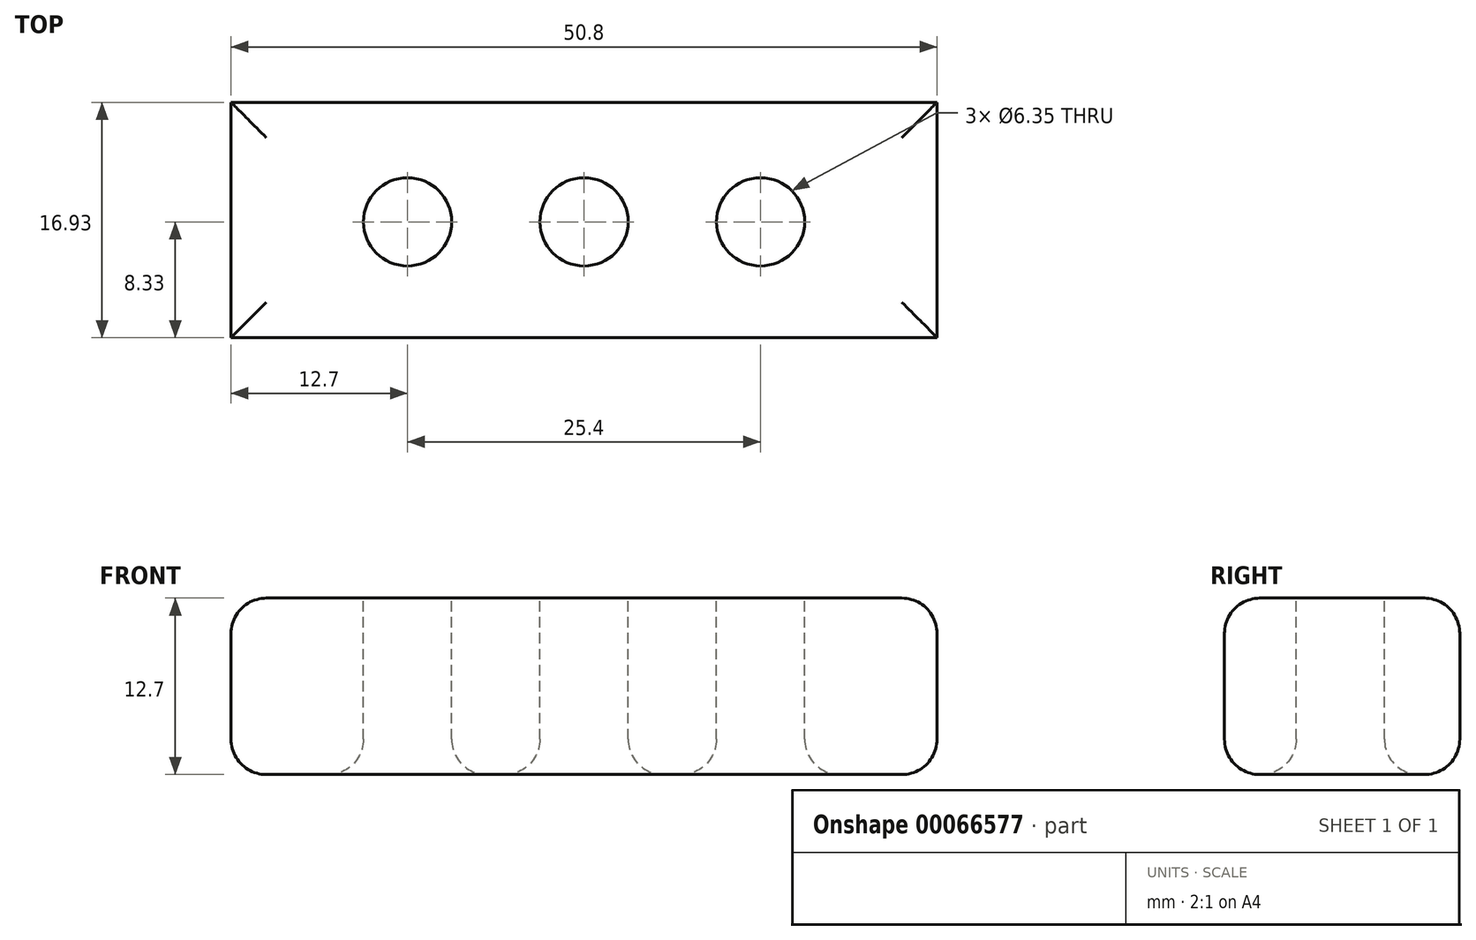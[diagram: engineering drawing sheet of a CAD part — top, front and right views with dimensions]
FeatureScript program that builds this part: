
annotation { "Feature Type Name" : "Feature", "Feature Type Description" : "" }
export const myFeature = defineFeature(function(context is Context, id is Id, definition is map)
    precondition{}
    {
        {
            var Q0;
            Q0=qCreatedBy(makeId("Top.planeOp"),FACE);
            var sketch = newSketch(context, id + "F0", { "sketchPlane" : qUnion([Q0])});
            skLineSegment(sketch, "E0.bottom", {"start": v(-25.4, 8.6) * mm, "end": v(25.4, 8.6) * mm});
            skLineSegment(sketch, "E0.top", {"start": v(-25.4, -8.33) * mm, "end": v(25.4, -8.33) * mm});
            skLineSegment(sketch, "E0.left", {"start": v(-25.4, 8.6) * mm, "end": v(-25.4, -8.33) * mm});
            skLineSegment(sketch, "E0.right", {"start": v(25.4, 8.6) * mm, "end": v(25.4, -8.33) * mm});
            skSolve(sketch);
        }
        {
            var Q0;
            Q0 = qSketchRegion(id + "F0", true);
            extrude(context, id + "F1", {"entities" : qUnion([Q0]), "depth" : 12.7 * mm, "offsetDistance" : 25.4 * mm});
        }
        {
            var Q0;
            Q0=makeQuery(id+"F1.opExtrude","CAP_FACE",FACE,{"disambiguationData":[OSD([sQuery(id+"F0.wireOp",EDGE,"E0.bottom"),sQuery(id+"F0.wireOp",EDGE,"E0.top"),sQuery(id+"F0.wireOp",EDGE,"E0.left"),sQuery(id+"F0.wireOp",EDGE,"E0.right")])],"isStart":false});
            var sketch = newSketch(context, id + "F2", { "sketchPlane" : qUnion([Q0])});
            skCircle(sketch, "E1", {"center": v(-12.7, 0) * mm, "radius": 3.18 * mm});
            skCircle(sketch, "E2", {"center": v(0, 0) * mm, "radius": 3.18 * mm});
            skCircle(sketch, "E3", {"center": v(12.7, 0) * mm, "radius": 3.18 * mm});
            skSolve(sketch);
        }
        {
            var Q0;
            Q0 = qSketchRegion(id + "F2", true);
            extrude(context, id + "F3", {"entities" : qUnion([Q0]), "operationType" : NewBodyOperationType.REMOVE, "oppositeDirection" : true, "depth" : 25.4 * mm});
        }
        {
            var Q0;
            Q0=makeQuery(id+"F3.boolean.opBoolean","COPY",EDGE,{"derivedFrom":makeQuery(id+"F3.opExtrude","CAP_EDGE",EDGE,{"disambiguationData":[OSD([sQuery(id+"F2.wireOp",EDGE,"E1")])],"isStart":true})});
            var Q1;
            Q1=makeQuery(id+"F3.boolean.opBoolean","COPY",EDGE,{"derivedFrom":makeQuery(id+"F3.opExtrude","CAP_EDGE",EDGE,{"disambiguationData":[OSD([sQuery(id+"F2.wireOp",EDGE,"E2")])],"isStart":true})});
            var Q2;
            Q2=makeQuery(id+"F3.boolean.opBoolean","COPY",EDGE,{"derivedFrom":makeQuery(id+"F3.opExtrude","CAP_EDGE",EDGE,{"disambiguationData":[OSD([sQuery(id+"F2.wireOp",EDGE,"E3")])],"isStart":true})});
            var Q3;
            Q3=makeQuery(id+"F3.boolean.opBoolean","COPY",EDGE,{"derivedFrom":makeQuery(id+"F3.opExtrude","CAP_EDGE",EDGE,{"disambiguationData":[OSD([sQuery(id+"F2.wireOp",EDGE,"E1")])],"isStart":false})});
            var Q4;
            Q4=makeQuery(id+"F3.boolean.opBoolean","COPY",EDGE,{"derivedFrom":makeQuery(id+"F3.opExtrude","CAP_EDGE",EDGE,{"disambiguationData":[OSD([sQuery(id+"F2.wireOp",EDGE,"E2")])],"isStart":false})});
            var Q5;
            Q5=makeQuery(id+"F3.boolean.opBoolean","COPY",EDGE,{"derivedFrom":makeQuery(id+"F3.opExtrude","CAP_EDGE",EDGE,{"disambiguationData":[OSD([sQuery(id+"F2.wireOp",EDGE,"E3")])],"isStart":false})});
            var Q6;
            Q6=makeQuery(id+"F3.boolean.opBoolean","INTERSECT",EDGE,{"derivedFrom":[makeQuery(id+"F1.opExtrude","CAP_FACE",FACE,{"disambiguationData":[OSD([sQuery(id+"F0.wireOp",EDGE,"E0.bottom"),sQuery(id+"F0.wireOp",EDGE,"E0.top"),sQuery(id+"F0.wireOp",EDGE,"E0.left"),sQuery(id+"F0.wireOp",EDGE,"E0.right")])],"isStart":true}),makeQuery(id+"F3.opExtrude","SWEPT_FACE",FACE,{"disambiguationData":[OSD([sQuery(id+"F2.wireOp",EDGE,"E1")])]})]});
            var Q7;
            Q7=makeQuery(id+"F3.boolean.opBoolean","INTERSECT",EDGE,{"derivedFrom":[makeQuery(id+"F1.opExtrude","CAP_FACE",FACE,{"disambiguationData":[OSD([sQuery(id+"F0.wireOp",EDGE,"E0.bottom"),sQuery(id+"F0.wireOp",EDGE,"E0.top"),sQuery(id+"F0.wireOp",EDGE,"E0.left"),sQuery(id+"F0.wireOp",EDGE,"E0.right")])],"isStart":true}),makeQuery(id+"F3.opExtrude","SWEPT_FACE",FACE,{"disambiguationData":[OSD([sQuery(id+"F2.wireOp",EDGE,"E2")])]})]});
            var Q8;
            Q8=makeQuery(id+"F3.boolean.opBoolean","INTERSECT",EDGE,{"derivedFrom":[makeQuery(id+"F1.opExtrude","CAP_FACE",FACE,{"disambiguationData":[OSD([sQuery(id+"F0.wireOp",EDGE,"E0.bottom"),sQuery(id+"F0.wireOp",EDGE,"E0.top"),sQuery(id+"F0.wireOp",EDGE,"E0.left"),sQuery(id+"F0.wireOp",EDGE,"E0.right")])],"isStart":true}),makeQuery(id+"F3.opExtrude","SWEPT_FACE",FACE,{"disambiguationData":[OSD([sQuery(id+"F2.wireOp",EDGE,"E3")])]})]});
            fillet(context, id + "F4", {"entities" : qUnion([Q0, Q1, Q2, Q3, Q4, Q5, Q6, Q7, Q8]), "radius" : 2.54 * mm, "allowEdgeOverflow" : false});
        }
        {
            var Q0;
            Q0=makeQuery(id+"F1.opExtrude","CAP_EDGE",EDGE,{"disambiguationData":[OSD([sQuery(id+"F0.wireOp",EDGE,"E0.bottom")])],"isStart":false});
            var Q1;
            Q1=makeQuery(id+"F1.opExtrude","CAP_EDGE",EDGE,{"disambiguationData":[OSD([sQuery(id+"F0.wireOp",EDGE,"E0.right")])],"isStart":false});
            var Q2;
            Q2=makeQuery(id+"F1.opExtrude","CAP_EDGE",EDGE,{"disambiguationData":[OSD([sQuery(id+"F0.wireOp",EDGE,"E0.top")])],"isStart":false});
            var Q3;
            Q3=makeQuery(id+"F1.opExtrude","CAP_EDGE",EDGE,{"disambiguationData":[OSD([sQuery(id+"F0.wireOp",EDGE,"E0.left")])],"isStart":false});
            var Q4;
            Q4=makeQuery(id+"F1.opExtrude","CAP_EDGE",EDGE,{"disambiguationData":[OSD([sQuery(id+"F0.wireOp",EDGE,"E0.bottom")])],"isStart":true});
            var Q5;
            Q5=makeQuery(id+"F1.opExtrude","CAP_EDGE",EDGE,{"disambiguationData":[OSD([sQuery(id+"F0.wireOp",EDGE,"E0.left")])],"isStart":true});
            var Q6;
            Q6=makeQuery(id+"F1.opExtrude","CAP_EDGE",EDGE,{"disambiguationData":[OSD([sQuery(id+"F0.wireOp",EDGE,"E0.top")])],"isStart":true});
            var Q7;
            Q7=makeQuery(id+"F1.opExtrude","CAP_EDGE",EDGE,{"disambiguationData":[OSD([sQuery(id+"F0.wireOp",EDGE,"E0.right")])],"isStart":true});
            fillet(context, id + "F5", {"entities" : qUnion([Q0, Q1, Q2, Q3, Q4, Q5, Q6, Q7]), "radius" : 2.54 * mm, "tangentPropagation" : true, "allowEdgeOverflow" : false});
        }
    });
